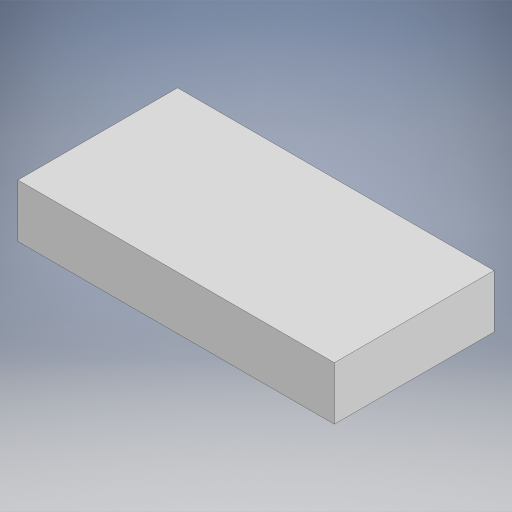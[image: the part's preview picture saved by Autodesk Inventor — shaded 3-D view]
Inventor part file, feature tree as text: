
AUTODESK INVENTOR PART (.ipt)
format: ipt  version: 2023 (Build 270158000, 158)  size: 211,456 bytes
history: native  units: in
note: dims shown in document units (in); Inventor stores cm internally (conversion verified against a paired STEP export)
features: extrude x1, sketch x1
ambient origin geometry x8: Origin, YZ Plane, XZ Plane, XY Plane, X Axis, Y Axis, Z Axis, Center Point
bodies: Body1 (feature_tree)
feature tree (2):
  extrude  "Extrusion2"  Depth=18.0in
  sketch  "Sketch2"  dims[d4=6.0in d5=18.0in d6=35.675in d7=0.0in]
